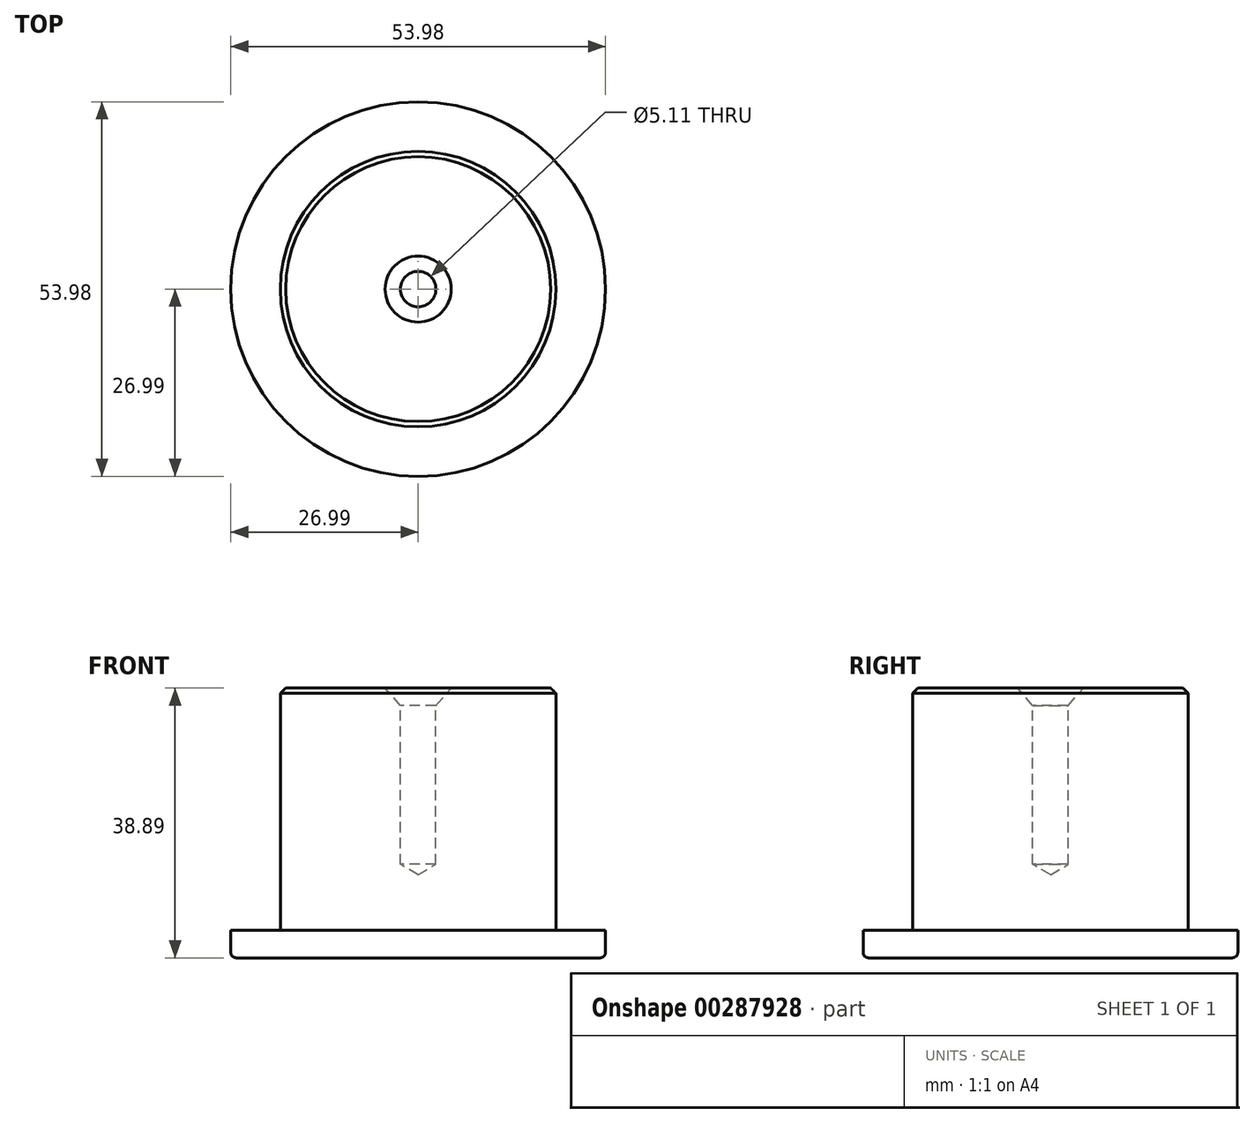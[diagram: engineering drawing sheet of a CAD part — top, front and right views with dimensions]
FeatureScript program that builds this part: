
annotation { "Feature Type Name" : "Feature", "Feature Type Description" : "" }
export const myFeature = defineFeature(function(context is Context, id is Id, definition is map)
    precondition{}
    {
        {
            var Q0;
            Q0=qCreatedBy(makeId("Top.planeOp"),FACE);
            var sketch = newSketch(context, id + "F0", { "sketchPlane" : qUnion([Q0])});
            skCircle(sketch, "E0", {"center": v(0, 0) * mm, "radius": 26.99 * mm});
            skCircle(sketch, "E1", {"center": v(0, 0) * mm, "radius": 19.84 * mm});
            skSolve(sketch);
        }
        {
            var Q0;
            Q0=makeQuery(id+"F0.imprint","IMPRINT",FACE,{"disambiguationData":[TD([[makeQuery(id+"F0.imprint","IMPRINT",EDGE,{"derivedFrom":sQuery(id+"F0.wireOp",EDGE,"E0")}),1.0]])]});
            extrude(context, id + "F1", {"entities" : qUnion([Q0]), "depth" : 3.96 * mm, "offsetDistance" : 25.4 * mm});
        }
        {
            var Q0;
            Q0=makeQuery(id+"F0.imprint","IMPRINT",FACE,{"disambiguationData":[TD([[makeQuery(id+"F0.imprint","IMPRINT",EDGE,{"derivedFrom":sQuery(id+"F0.wireOp",EDGE,"E1")}),1.0]])]});
            extrude(context, id + "F2", {"entities" : qUnion([Q0]), "operationType" : NewBodyOperationType.ADD, "depth" : 38.9 * mm, "offsetDistance" : 25.4 * mm});
        }
        {
            var Q0;
            Q0=makeQuery(id+"F1.opExtrude","CAP_EDGE",EDGE,{"disambiguationData":[OSD([sQuery(id+"F0.wireOp",EDGE,"E0")])],"isStart":true});
            fillet(context, id + "F3", {"entities" : qUnion([Q0]), "radius" : 0.79 * mm, "tangentPropagation" : true, "allowEdgeOverflow" : false});
        }
        {
            var Q0;
            Q0=makeQuery(id+"F2.opExtrude","CAP_EDGE",EDGE,{"disambiguationData":[OSD([sQuery(id+"F0.wireOp",EDGE,"E1")])],"isStart":false});
            chamfer(context, id + "F4", {"entities" : qUnion([Q0]), "chamferType" : ChamferType.OFFSET_ANGLE, "width" : 0.76 * mm, "oppositeDirection" : false, "angle" : 45 * degree, "tangentPropagation" : true});
        }
        {
            var Q0;
            Q0=makeQuery(id+"F2.opExtrude","CAP_FACE",FACE,{"disambiguationData":[OSD([sQuery(id+"F0.wireOp",EDGE,"E1")])],"isStart":false});
            var sketch = newSketch(context, id + "F5", { "sketchPlane" : qUnion([Q0])});
            skPoint(sketch, "E2", {"position": v(0, 0) * mm});
            skSolve(sketch);
        }
        {
            var Q0;
            Q0=sQuery(id+"F5.wireOp",VERTEX,"E2");
            var Q1;
            Q1=makeQuery(id+"F1.opExtrude","SWEPT_BODY",BODY,{"disambiguationData":[OSD([sQuery(id+"F0.wireOp",EDGE,"E0"),sQuery(id+"F0.wireOp",EDGE,"E1")])]});
            hole(context, id + "F6", {"style" : HoleStyle.C_SINK, "endStyle" : HoleEndStyle.BLIND, "holeDiameter" : 5.1 * mm, "cSinkDiameter" : 9.52 * mm, "cSinkAngle" : 82 * degree, "majorDiameter" : 6.35 * mm, "holeDepth" : 25.4 * mm, "isTappedThrough" : true, "tappedDepth" : 21.59 * mm, "tapClearance" : 3, "locations" : qUnion([Q0]), "scope" : qUnion([Q1])});
        }
    });
